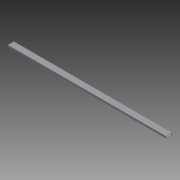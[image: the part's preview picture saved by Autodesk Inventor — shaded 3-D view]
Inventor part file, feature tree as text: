
AUTODESK INVENTOR PART (.ipt)
format: ipt  version: 2013 (Build 170138000, 138)  size: 79,360 bytes
history: native  units: in
note: dims shown in document units (in); Inventor stores cm internally (conversion verified against a paired STEP export)
features: other x2, extrude x1, sketch x1
ambient origin geometry x8: Origin, YZ Plane, XZ Plane, XY Plane, X Axis, Y Axis, Z Axis, Center Point
bodies: Solid1 (feature_tree)
feature tree (4):
  other  "Table"
  other  "squareTube_1x2-01"
  extrude  "Extrusion1"  Depth=3.0in
  sketch  "Sketch1"  dims[d0=1.0in d1=3.0in d2=0.125in d4=0.0in]
